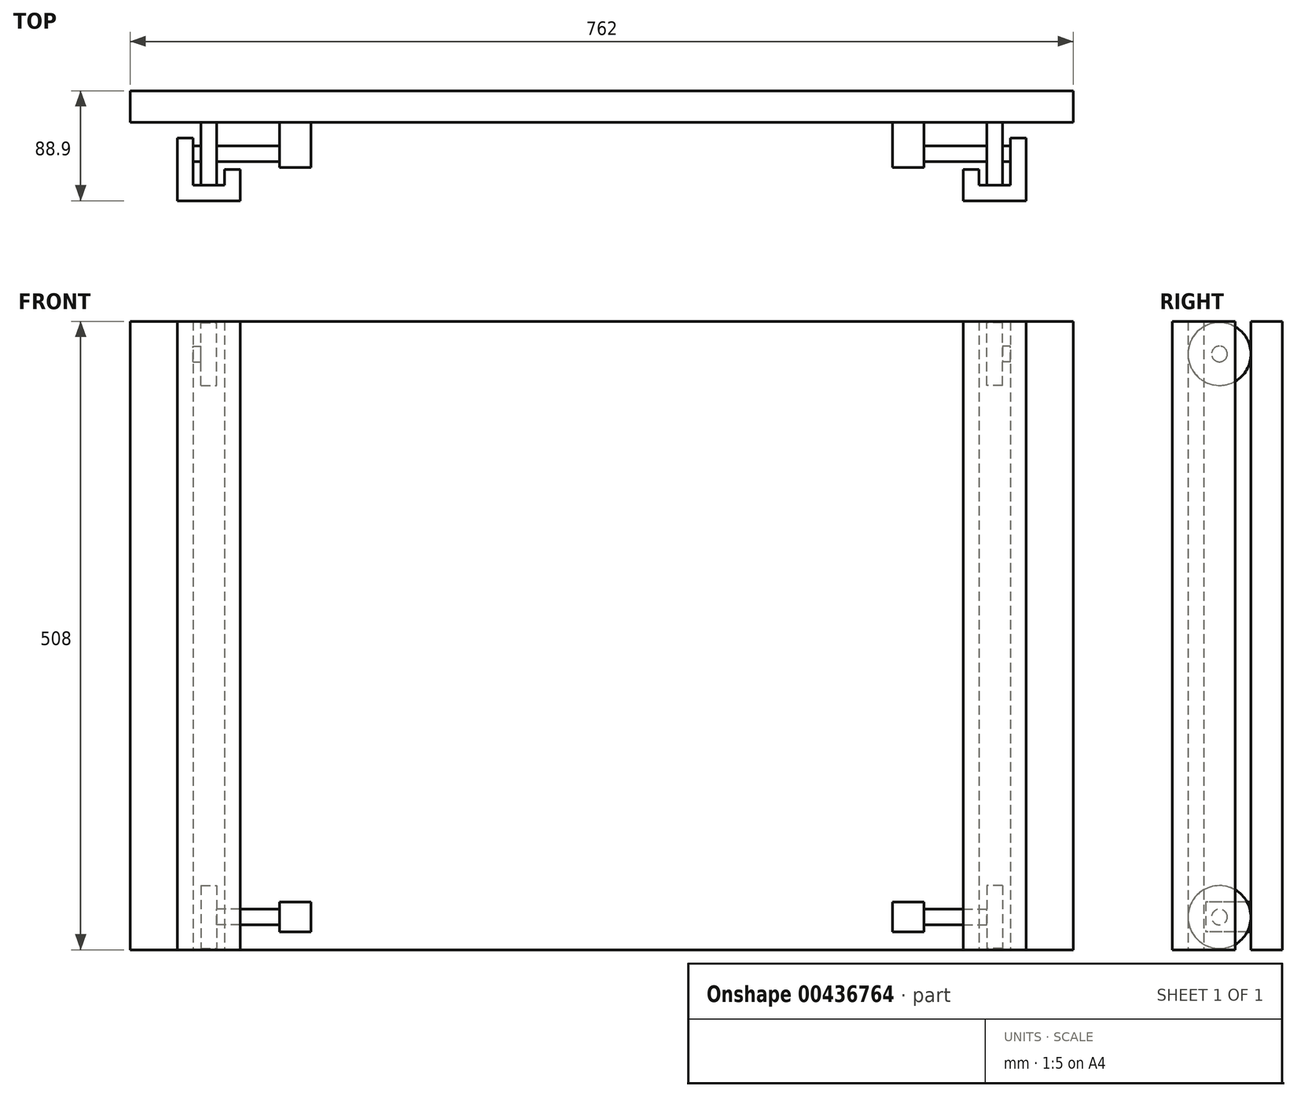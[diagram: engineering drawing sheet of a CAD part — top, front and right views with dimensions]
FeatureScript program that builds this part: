
annotation { "Feature Type Name" : "Feature", "Feature Type Description" : "" }
export const myFeature = defineFeature(function(context is Context, id is Id, definition is map)
    precondition{}
    {
        {
            var Q0;
            Q0=qCreatedBy(makeId("Top.planeOp"),FACE);
            var sketch = newSketch(context, id + "F0", { "sketchPlane" : qUnion([Q0])});
            skLineSegment(sketch, "E0.bottom", {"start": v(0, 0) * mm, "end": v(762, 0) * mm});
            skLineSegment(sketch, "E0.top", {"start": v(0, -25.4) * mm, "end": v(762, -25.4) * mm});
            skLineSegment(sketch, "E0.left", {"start": v(0, 0) * mm, "end": v(0, -25.4) * mm});
            skLineSegment(sketch, "E0.right", {"start": v(762, 0) * mm, "end": v(762, -25.4) * mm});
            skLineSegment(sketch, "E1", {"start": v(38.1, -88.9) * mm, "end": v(88.9, -88.9) * mm});
            skLineSegment(sketch, "E2", {"start": v(88.9, -88.9) * mm, "end": v(88.9, -63.5) * mm});
            skLineSegment(sketch, "E3", {"start": v(88.9, -63.5) * mm, "end": v(76.2, -63.5) * mm});
            skLineSegment(sketch, "E4", {"start": v(76.2, -63.5) * mm, "end": v(76.2, -76.2) * mm});
            skLineSegment(sketch, "E5", {"start": v(76.2, -76.2) * mm, "end": v(50.8, -76.2) * mm});
            skLineSegment(sketch, "E6", {"start": v(381, 101.75) * mm, "end": v(381, -179.22) * mm});
            skPoint(sketch, "E6.startSnap0", {"position": v(381, 0) * mm});
            skPoint(sketch, "E6.endSnap0", {"position": v(381, -25.4) * mm});
            skLineSegment(sketch, "E7.MirrorCS", {"start": v(762, -25.4) * mm, "end": v(0, -25.4) * mm});
            skLineSegment(sketch, "E8.MirrorCS", {"start": v(762, 0) * mm, "end": v(0, 0) * mm});
            skLineSegment(sketch, "E9", {"start": v(38.1, -88.9) * mm, "end": v(38.1, -38.1) * mm});
            skLineSegment(sketch, "E10", {"start": v(38.1, -38.1) * mm, "end": v(50.8, -38.1) * mm});
            skLineSegment(sketch, "E11", {"start": v(50.8, -38.1) * mm, "end": v(50.8, -76.2) * mm});
            skLineSegment(sketch, "E12.MirrorCS", {"start": v(673.1, -63.5) * mm, "end": v(685.8, -63.5) * mm});
            skLineSegment(sketch, "E13.MirrorCS", {"start": v(685.8, -63.5) * mm, "end": v(685.8, -76.2) * mm});
            skLineSegment(sketch, "E14.MirrorCS", {"start": v(685.8, -76.2) * mm, "end": v(711.2, -76.2) * mm});
            skLineSegment(sketch, "E15.MirrorCS", {"start": v(723.9, -88.9) * mm, "end": v(673.1, -88.9) * mm});
            skLineSegment(sketch, "E16.MirrorCS", {"start": v(723.9, -38.1) * mm, "end": v(711.2, -38.1) * mm});
            skLineSegment(sketch, "E17.MirrorCS", {"start": v(673.1, -88.9) * mm, "end": v(673.1, -63.5) * mm});
            skLineSegment(sketch, "E18.MirrorCS", {"start": v(711.2, -38.1) * mm, "end": v(711.2, -76.2) * mm});
            skLineSegment(sketch, "E19.MirrorCS", {"start": v(723.9, -88.9) * mm, "end": v(723.9, -38.1) * mm});
            skSolve(sketch);
        }
        {
            var Q0;
            {var subQ0=sQuery(id+"F0.wireOp",EDGE,"E0.left");Q0=makeQuery(id+"F0.imprint","IMPRINT",FACE,{"disambiguationData":[TD([[makeQuery(id+"F0.imprint","IMPRINT",EDGE,{"derivedFrom":subQ0}),1.0]])]});}
            var Q1;
            Q1=makeQuery(id+"F0.imprint","IMPRINT",FACE,{"disambiguationData":[TD([[makeQuery(id+"F0.imprint","IMPRINT",EDGE,{"derivedFrom":sQuery(id+"F0.wireOp",EDGE,"E1")}),1.0]])]});
            var Q2;
            {var subQ5=sQuery(id+"F0.wireOp",EDGE,"E0.right");Q2=makeQuery(id+"F0.imprint","IMPRINT",FACE,{"disambiguationData":[TD([[makeQuery(id+"F0.imprint","IMPRINT",EDGE,{"derivedFrom":subQ5}),-1.0]])]});}
            var Q3;
            Q3=makeQuery(id+"F0.imprint","IMPRINT",FACE,{"disambiguationData":[TD([[makeQuery(id+"F0.imprint","IMPRINT",EDGE,{"derivedFrom":sQuery(id+"F0.wireOp",EDGE,"E12.MirrorCS")}),-1.0]])]});
            extrude(context, id + "F1", {"entities" : qUnion([Q0, Q1, Q2, Q3]), "depth" : 508 * mm});
        }
        {
            var Q0;
            Q0=makeQuery(id+"F1.opExtrude","SWEPT_FACE",FACE,{"disambiguationData":[OSD([sQuery(id+"F0.wireOp",EDGE,"E0.left")])]});
            cPlane(context, id + "F2", {"entities" : qUnion([Q0]), "cplaneType" : CPlaneType.OFFSET, "offset" : 63.5 * mm, "oppositeDirection" : true, "width" : 152.4 * mm, "height" : 152.4 * mm});
        }
        {
            var Q0;
            Q0=qCreatedBy(id+"F2.planeOp",FACE);
            var sketch = newSketch(context, id + "F3", { "sketchPlane" : qUnion([Q0])});
            skCircle(sketch, "E20", {"center": v(50.8, 26.45) * mm, "radius": 25.4 * mm});
            skSolve(sketch);
        }
        {
            var Q0;
            Q0=makeQuery(id+"F3.imprint","IMPRINT",FACE,{"disambiguationData":[TD([[makeQuery(id+"F3.imprint","IMPRINT",EDGE,{"derivedFrom":sQuery(id+"F3.wireOp",EDGE,"E20")}),1.0]])]});
            extrude(context, id + "F4", {"entities" : qUnion([Q0]), "endBound" : BoundingType.SYMMETRIC, "depth" : 12.7 * mm});
        }
        {
            var Q0;
            Q0=makeQuery(id+"F1.opExtrude","SWEPT_FACE",FACE,{"disambiguationData":[OSD([sQuery(id+"F0.wireOp",EDGE,"E0.left")])]});
            var Q1;
            Q1=makeQuery(id+"F1.opExtrude","SWEPT_FACE",FACE,{"disambiguationData":[OSD([sQuery(id+"F0.wireOp",EDGE,"E0.right")])]});
            cPlane(context, id + "F5", {"entities" : qUnion([Q0, Q1]), "cplaneType" : CPlaneType.MID_PLANE, "offset" : 25.4 * mm, "width" : 152.4 * mm, "height" : 152.4 * mm});
        }
        {
            var Q0;
            Q0=makeQuery(id+"F4.opExtrude","SWEPT_BODY",BODY,{"disambiguationData":[OSD([sQuery(id+"F3.wireOp",EDGE,"E20")])]});
            var Q1;
            Q1=makeQuery(id+"F1.opExtrude","SWEPT_BODY",BODY,{"disambiguationData":[OSD([sQuery(id+"F0.wireOp",EDGE,"E1"),sQuery(id+"F0.wireOp",EDGE,"E2"),sQuery(id+"F0.wireOp",EDGE,"E3"),sQuery(id+"F0.wireOp",EDGE,"E4"),sQuery(id+"F0.wireOp",EDGE,"E5"),sQuery(id+"F0.wireOp",EDGE,"E9"),sQuery(id+"F0.wireOp",EDGE,"E10"),sQuery(id+"F0.wireOp",EDGE,"E11")])]});
            var Q2;
            Q2=qCreatedBy(id+"F5.planeOp",FACE);
            mirror(context, id + "F6", {"entities" : qUnion([Q0, Q1]), "mirrorPlane" : qUnion([Q2])});
        }
        {
            var Q0;
            Q0=makeQuery(id+"F1.opExtrude","CAP_FACE",FACE,{"disambiguationData":[OSD([sQuery(id+"F0.wireOp",EDGE,"E0.left"),sQuery(id+"F0.wireOp",EDGE,"E0.right"),sQuery(id+"F0.wireOp",EDGE,"E0.bottom"),sQuery(id+"F0.wireOp",EDGE,"E0.top")])],"isStart":true});
            var Q1;
            Q1=makeQuery(id+"F1.opExtrude","CAP_FACE",FACE,{"disambiguationData":[OSD([sQuery(id+"F0.wireOp",EDGE,"E0.left"),sQuery(id+"F0.wireOp",EDGE,"E0.right"),sQuery(id+"F0.wireOp",EDGE,"E0.bottom"),sQuery(id+"F0.wireOp",EDGE,"E0.top")])],"isStart":false});
            cPlane(context, id + "F7", {"entities" : qUnion([Q0, Q1]), "cplaneType" : CPlaneType.MID_PLANE, "offset" : 25.4 * mm, "width" : 152.4 * mm, "height" : 152.4 * mm});
        }
        {
            var Q0;
            Q0=makeQuery(id+"F4.opExtrude","SWEPT_BODY",BODY,{"disambiguationData":[OSD([sQuery(id+"F3.wireOp",EDGE,"E20")])]});
            var Q1;
            Q1=makeQuery(id+"F6.opPattern","COPY",BODY,{"derivedFrom":makeQuery(id+"F4.opExtrude","SWEPT_BODY",BODY,{"disambiguationData":[OSD([sQuery(id+"F3.wireOp",EDGE,"E20")])]}),"instanceName":"1"});
            var Q2;
            Q2=qCreatedBy(id+"F7.planeOp",FACE);
            mirror(context, id + "F8", {"entities" : qUnion([Q0, Q1]), "mirrorPlane" : qUnion([Q2])});
        }
        {
            var Q0;
            Q0=makeQuery(id+"F4.opExtrude","CAP_FACE",FACE,{"disambiguationData":[OSD([sQuery(id+"F3.wireOp",EDGE,"E20")])],"isStart":true});
            cPlane(context, id + "F9", {"entities" : qUnion([Q0]), "cplaneType" : CPlaneType.OFFSET, "offset" : 0 * mm, "width" : 152.4 * mm, "height" : 152.4 * mm});
        }
        {
            var Q0;
            Q0=qCreatedBy(id+"F9.planeOp",FACE);
            var sketch = newSketch(context, id + "F10", { "sketchPlane" : qUnion([Q0])});
            skCircle(sketch, "E21", {"center": v(-50.8, 26.45) * mm, "radius": 6.35 * mm});
            skSolve(sketch);
        }
        {
            var Q0;
            Q0 = qSketchRegion(id + "F10", true);
            extrude(context, id + "F11", {"entities" : qUnion([Q0]), "operationType" : NewBodyOperationType.ADD, "depth" : 50.8 * mm});
        }
        {
            var Q0;
            Q0=makeQuery(id+"F11.opExtrude","CAP_FACE",FACE,{"disambiguationData":[OSD([sQuery(id+"F10.wireOp",EDGE,"E21")])],"isStart":false});
            cPlane(context, id + "F12", {"entities" : qUnion([Q0]), "cplaneType" : CPlaneType.OFFSET, "offset" : 0 * mm, "width" : 152.4 * mm, "height" : 152.4 * mm});
        }
        {
            var Q0;
            Q0=qCreatedBy(id+"F12.planeOp",FACE);
            var sketch = newSketch(context, id + "F13", { "sketchPlane" : qUnion([Q0])});
            skLineSegment(sketch, "E22.bottom", {"start": v(-25.47, 38.76) * mm, "end": v(-61.99, 38.76) * mm});
            skLineSegment(sketch, "E22.top", {"start": v(-25.47, 14.63) * mm, "end": v(-61.99, 14.63) * mm});
            skLineSegment(sketch, "E22.left", {"start": v(-25.47, 38.76) * mm, "end": v(-25.47, 14.63) * mm});
            skLineSegment(sketch, "E22.right", {"start": v(-61.99, 38.76) * mm, "end": v(-61.99, 14.63) * mm});
            skPoint(sketch, "E22.middle", {"position": v(-43.73, 26.7) * mm});
            skSolve(sketch);
        }
        {
            var Q0;
            Q0 = qSketchRegion(id + "F13", true);
            extrude(context, id + "F14", {"entities" : qUnion([Q0]), "operationType" : NewBodyOperationType.ADD, "depth" : 25.4 * mm});
        }
        {
            var Q0;
            Q0=makeQuery(id+"F4.opExtrude","SWEPT_BODY",BODY,{"disambiguationData":[OSD([sQuery(id+"F3.wireOp",EDGE,"E20")])]});
            var Q1;
            Q1=makeQuery(id+"F8.opPattern","COPY",BODY,{"derivedFrom":makeQuery(id+"F4.opExtrude","SWEPT_BODY",BODY,{"disambiguationData":[OSD([sQuery(id+"F3.wireOp",EDGE,"E20")])]}),"instanceName":"1"});
            var Q2;
            Q2=qCreatedBy(id+"F5.planeOp",FACE);
            mirror(context, id + "F15", {"entities" : qUnion([Q0, Q1]), "mirrorPlane" : qUnion([Q2])});
        }
        {
            var Q0;
            Q0=makeQuery(id+"F1.opExtrude","SWEPT_FACE",FACE,{"disambiguationData":[OSD([sQuery(id+"F0.wireOp",EDGE,"E0.left")])]});
            cPlane(context, id + "F16", {"entities" : qUnion([Q0]), "cplaneType" : CPlaneType.OFFSET, "offset" : 57.15 * mm, "oppositeDirection" : true, "width" : 152.4 * mm, "height" : 152.4 * mm});
        }
        {
            var Q0;
            Q0=qCreatedBy(id+"F16.planeOp",FACE);
            var sketch = newSketch(context, id + "F17", { "sketchPlane" : qUnion([Q0])});
            skCircle(sketch, "E23", {"center": v(50.8, 481.55) * mm, "radius": 6.35 * mm});
            skSolve(sketch);
        }
        {
            var Q0;
            Q0 = qSketchRegion(id + "F17", true);
            var Q1;
            Q1=makeQuery(id+"F1.opExtrude","SWEPT_FACE",FACE,{"disambiguationData":[OSD([sQuery(id+"F0.wireOp",EDGE,"E11")])]});
            extrude(context, id + "F18", {"entities" : qUnion([Q0]), "endBound" : BoundingType.UP_TO_SURFACE, "endBoundEntityFace" : qUnion([Q1]), "depth" : 25.4 * mm});
        }
        {
            var Q0;
            Q0=makeQuery(id+"F18.opExtrude","SWEPT_BODY",BODY,{"disambiguationData":[OSD([sQuery(id+"F17.wireOp",EDGE,"E23")])]});
            var Q1;
            Q1=qCreatedBy(id+"F5.planeOp",FACE);
            mirror(context, id + "F19", {"entities" : qUnion([Q0]), "mirrorPlane" : qUnion([Q1])});
        }
    });
